# Revit family: PL80110
name_source: partatom
category: Furniture
units: mm (PartAtom-declared; Revit-internal decimal feet)

## family parameters
Always vertical = Yes
Cut with Voids When Loaded = No
OmniClass Number = 23.40.20.00
OmniClass Title = General Furniture and Specialties
Room Calculation Point = No
Shared = No
Work Plane-Based = No

## types (1)
- PL80110
    Default Elevation = 0 mm  [stored 0 ft]
    Depth = 480 mm  [stored 1.5748 ft]
    Description = Trestle wooden leg for Plania range available in Solid Oak or Solid Walnut finish. Assembly required
    Height = 450 mm  [stored 1.47638 ft]
    Leg Finish = Wood - Oak - Natural - V
    Manufacturer = Sandler
    Model = PL80110
    URL = https://www.sandlerseating.com
    Width = 84 mm  [stored 0.275591 ft]

note: [stored X ft] marks values corroborated as IEEE doubles in the binary element streams (Revit-internal decimal feet)

## geometry (parser evidence)
native form markers: Sweep x3
no freeform markers — native parametric forms only
